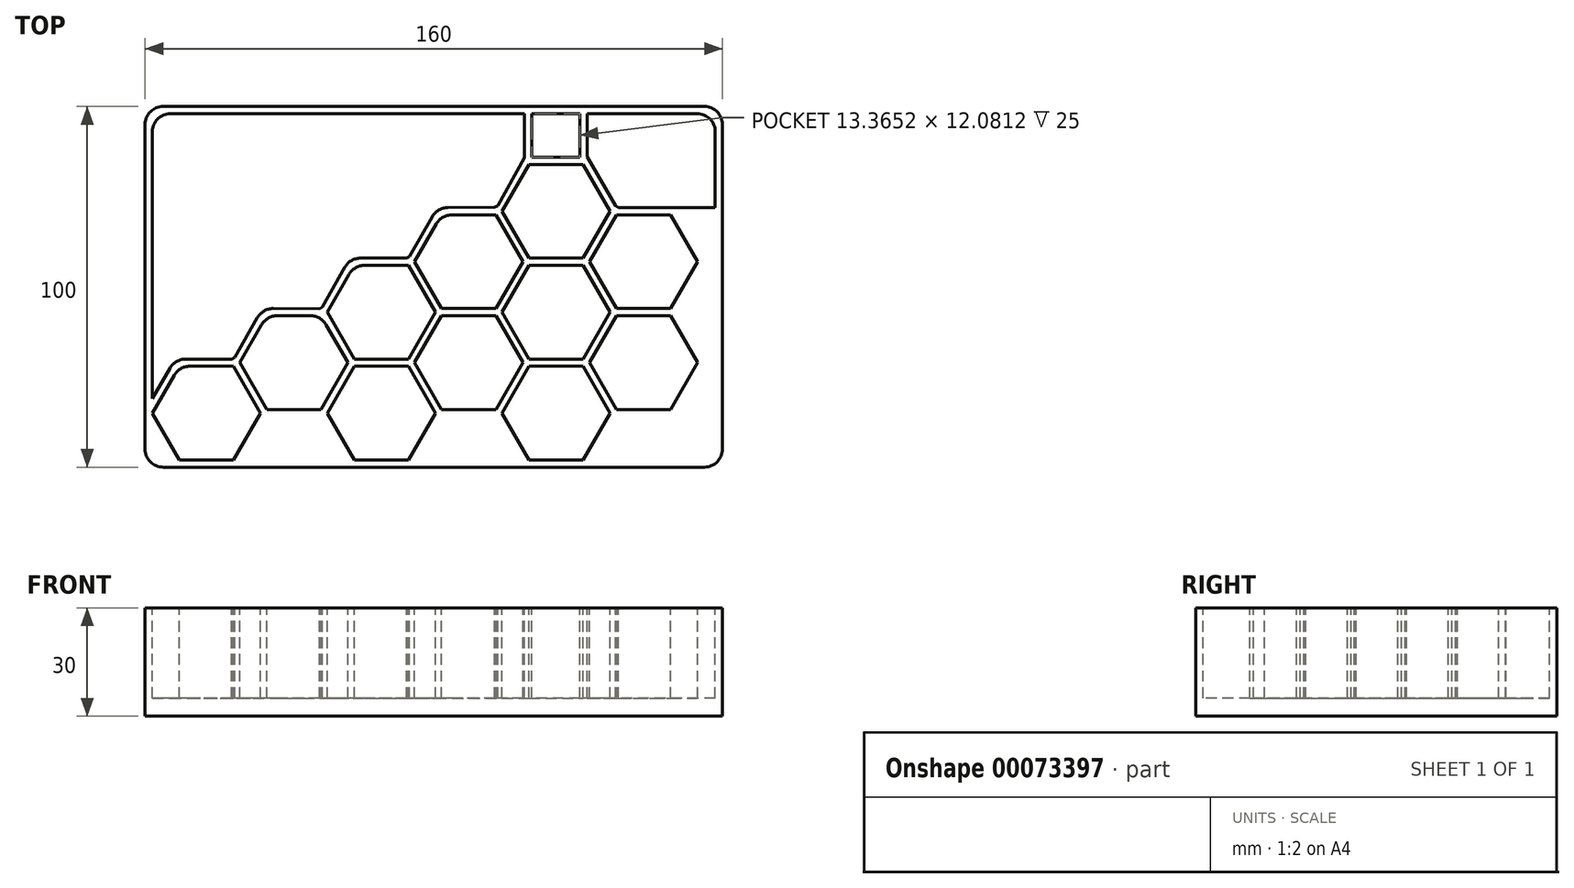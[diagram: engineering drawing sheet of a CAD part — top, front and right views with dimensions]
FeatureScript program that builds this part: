
annotation { "Feature Type Name" : "Feature", "Feature Type Description" : "" }
export const myFeature = defineFeature(function(context is Context, id is Id, definition is map)
    precondition{}
    {
        {
            var Q0;
            Q0=qCreatedBy(makeId("Top.planeOp"),FACE);
            var sketch = newSketch(context, id + "F0", { "sketchPlane" : qUnion([Q0])});
            skLineSegment(sketch, "E0.rect.bottom", {"start": v(80, 50) * mm, "end": v(-80, 50) * mm});
            skLineSegment(sketch, "E0.rect.top", {"start": v(80, -50) * mm, "end": v(-80, -50) * mm});
            skLineSegment(sketch, "E0.rect.left", {"start": v(80, 50) * mm, "end": v(80, -50) * mm});
            skLineSegment(sketch, "E0.rect.right", {"start": v(-80, 50) * mm, "end": v(-80, -50) * mm});
            skPoint(sketch, "E0.rect.middle", {"position": v(0, 0) * mm});
            skSolve(sketch);
        }
        {
            var Q0;
            Q0=makeQuery(id+"F0.imprint","IMPRINT",FACE,{"disambiguationData":[TD([[makeQuery(id+"F0.imprint","IMPRINT",EDGE,{"derivedFrom":sQuery(id+"F0.wireOp",EDGE,"E0.rect.bottom")}),1.0]])]});
            extrude(context, id + "F1", {"entities" : qUnion([Q0]), "depth" : 30 * mm});
        }
        {
            var Q0;
            Q0=makeQuery(id+"F1.opExtrude","CAP_FACE",FACE,{"disambiguationData":[OSD([sQuery(id+"F0.wireOp",EDGE,"E0.rect.bottom"),sQuery(id+"F0.wireOp",EDGE,"E0.rect.top"),sQuery(id+"F0.wireOp",EDGE,"E0.rect.left"),sQuery(id+"F0.wireOp",EDGE,"E0.rect.right")])],"isStart":false});
            var sketch = newSketch(context, id + "F2", { "sketchPlane" : qUnion([Q0])});
            skCircle(sketch, "E1.cCircle", {"center": v(-63, -35) * mm, "radius": 13 * mm, "construction": true});
            skLineSegment(sketch, "E1.0", {"start": v(-55.5, -48) * mm, "end": v(-70.5, -48) * mm});
            skLineSegment(sketch, "E1.1", {"start": v(-70.5, -48) * mm, "end": v(-78, -35) * mm});
            skLineSegment(sketch, "E1.2", {"start": v(-78, -35) * mm, "end": v(-70.5, -22.02) * mm});
            skLineSegment(sketch, "E1.3", {"start": v(-70.5, -22.02) * mm, "end": v(-55.5, -22.02) * mm});
            skLineSegment(sketch, "E1.4", {"start": v(-55.5, -22.02) * mm, "end": v(-48, -35) * mm});
            skLineSegment(sketch, "E1.5", {"start": v(-48, -35) * mm, "end": v(-55.5, -48) * mm});
            skPoint(sketch, "E1.0.midPoint", {"position": v(-63, -48) * mm});
            skLineSegment(sketch, "E2.0.1.0", {"start": v(-46.27, -8.03) * mm, "end": v(-31.27, -8.03) * mm});
            skLineSegment(sketch, "E2.0.1.1", {"start": v(-31.27, -8.03) * mm, "end": v(-23.77, -21.02) * mm});
            skLineSegment(sketch, "E2.0.1.2", {"start": v(-23.77, -21.02) * mm, "end": v(-31.27, -34) * mm});
            skLineSegment(sketch, "E2.0.1.3", {"start": v(-31.27, -34) * mm, "end": v(-46.27, -34) * mm});
            skLineSegment(sketch, "E2.0.1.4", {"start": v(-46.27, -34) * mm, "end": v(-53.77, -21.02) * mm});
            skLineSegment(sketch, "E2.0.1.5", {"start": v(-53.77, -21.02) * mm, "end": v(-46.27, -8.03) * mm});
            skLineSegment(sketch, "E2.0.2.0", {"start": v(-22.04, 5.96) * mm, "end": v(-7.04, 5.96) * mm});
            skLineSegment(sketch, "E2.0.2.1", {"start": v(-7.04, 5.96) * mm, "end": v(0.46, -7.03) * mm});
            skLineSegment(sketch, "E2.0.2.2", {"start": v(0.46, -7.03) * mm, "end": v(-7.04, -20.02) * mm});
            skLineSegment(sketch, "E2.0.2.3", {"start": v(-7.04, -20.02) * mm, "end": v(-22.04, -20.02) * mm});
            skLineSegment(sketch, "E2.0.2.4", {"start": v(-22.04, -20.02) * mm, "end": v(-29.54, -7.03) * mm});
            skLineSegment(sketch, "E2.0.2.5", {"start": v(-29.54, -7.03) * mm, "end": v(-22.04, 5.96) * mm});
            skLineSegment(sketch, "E2.0.3.0", {"start": v(2.2, 19.95) * mm, "end": v(17.2, 19.95) * mm});
            skLineSegment(sketch, "E2.0.3.1", {"start": v(17.2, 19.95) * mm, "end": v(24.7, 6.96) * mm});
            skLineSegment(sketch, "E2.0.3.2", {"start": v(24.7, 6.96) * mm, "end": v(17.2, -6.03) * mm});
            skLineSegment(sketch, "E2.0.3.3", {"start": v(17.2, -6.03) * mm, "end": v(2.2, -6.03) * mm});
            skLineSegment(sketch, "E2.0.3.4", {"start": v(2.2, -6.03) * mm, "end": v(-5.3, 6.96) * mm});
            skLineSegment(sketch, "E2.0.3.5", {"start": v(-5.3, 6.96) * mm, "end": v(2.2, 19.95) * mm});
            skLineSegment(sketch, "E2.0.4.0", {"start": v(26.43, 33.94) * mm, "end": v(41.43, 33.94) * mm});
            skLineSegment(sketch, "E2.0.4.1", {"start": v(41.43, 33.94) * mm, "end": v(48.93, 20.95) * mm});
            skLineSegment(sketch, "E2.0.4.2", {"start": v(48.93, 20.95) * mm, "end": v(41.43, 7.96) * mm});
            skLineSegment(sketch, "E2.0.4.3", {"start": v(41.43, 7.96) * mm, "end": v(26.43, 7.96) * mm});
            skLineSegment(sketch, "E2.0.4.4", {"start": v(26.43, 7.96) * mm, "end": v(18.93, 20.95) * mm});
            skLineSegment(sketch, "E2.0.4.5", {"start": v(18.93, 20.95) * mm, "end": v(26.43, 33.94) * mm});
            skLineSegment(sketch, "E2.1.0.0", {"start": v(-22.04, -22.02) * mm, "end": v(-7.04, -22.02) * mm});
            skLineSegment(sketch, "E2.1.0.1", {"start": v(-7.04, -22.02) * mm, "end": v(0.46, -35) * mm});
            skLineSegment(sketch, "E2.1.0.2", {"start": v(0.46, -35) * mm, "end": v(-7.04, -48) * mm});
            skLineSegment(sketch, "E2.1.0.3", {"start": v(-7.04, -48) * mm, "end": v(-22.04, -48) * mm});
            skLineSegment(sketch, "E2.1.0.4", {"start": v(-22.04, -48) * mm, "end": v(-29.54, -35) * mm});
            skLineSegment(sketch, "E2.1.0.5", {"start": v(-29.54, -35) * mm, "end": v(-22.04, -22.02) * mm});
            skLineSegment(sketch, "E2.1.1.0", {"start": v(2.2, -8.03) * mm, "end": v(17.2, -8.03) * mm});
            skLineSegment(sketch, "E2.1.1.1", {"start": v(17.2, -8.03) * mm, "end": v(24.7, -21.02) * mm});
            skLineSegment(sketch, "E2.1.1.2", {"start": v(24.7, -21.02) * mm, "end": v(17.2, -34) * mm});
            skLineSegment(sketch, "E2.1.1.3", {"start": v(17.2, -34) * mm, "end": v(2.2, -34) * mm});
            skLineSegment(sketch, "E2.1.1.4", {"start": v(2.2, -34) * mm, "end": v(-5.3, -21.02) * mm});
            skLineSegment(sketch, "E2.1.1.5", {"start": v(-5.3, -21.02) * mm, "end": v(2.2, -8.03) * mm});
            skLineSegment(sketch, "E2.1.2.0", {"start": v(26.43, 5.96) * mm, "end": v(41.43, 5.96) * mm});
            skLineSegment(sketch, "E2.1.2.1", {"start": v(41.43, 5.96) * mm, "end": v(48.93, -7.03) * mm});
            skLineSegment(sketch, "E2.1.2.2", {"start": v(48.93, -7.03) * mm, "end": v(41.43, -20.02) * mm});
            skLineSegment(sketch, "E2.1.2.3", {"start": v(41.43, -20.02) * mm, "end": v(26.43, -20.02) * mm});
            skLineSegment(sketch, "E2.1.2.4", {"start": v(26.43, -20.02) * mm, "end": v(18.93, -7.03) * mm});
            skLineSegment(sketch, "E2.1.2.5", {"start": v(18.93, -7.03) * mm, "end": v(26.43, 5.96) * mm});
            skLineSegment(sketch, "E2.1.3.0", {"start": v(50.66, 19.95) * mm, "end": v(65.66, 19.95) * mm});
            skLineSegment(sketch, "E2.1.3.1", {"start": v(65.66, 19.95) * mm, "end": v(73.16, 6.96) * mm});
            skLineSegment(sketch, "E2.1.3.2", {"start": v(73.16, 6.96) * mm, "end": v(65.66, -6.03) * mm});
            skLineSegment(sketch, "E2.1.3.3", {"start": v(65.66, -6.03) * mm, "end": v(50.66, -6.03) * mm});
            skLineSegment(sketch, "E2.1.3.4", {"start": v(50.66, -6.03) * mm, "end": v(43.16, 6.96) * mm});
            skLineSegment(sketch, "E2.1.3.5", {"start": v(43.16, 6.96) * mm, "end": v(50.66, 19.95) * mm});
            skLineSegment(sketch, "E2.2.0.0", {"start": v(26.43, -22.02) * mm, "end": v(41.43, -22.02) * mm});
            skLineSegment(sketch, "E2.2.0.1", {"start": v(41.43, -22.02) * mm, "end": v(48.93, -35) * mm});
            skLineSegment(sketch, "E2.2.0.2", {"start": v(48.93, -35) * mm, "end": v(41.43, -48) * mm});
            skLineSegment(sketch, "E2.2.0.3", {"start": v(41.43, -48) * mm, "end": v(26.43, -48) * mm});
            skLineSegment(sketch, "E2.2.0.4", {"start": v(26.43, -48) * mm, "end": v(18.93, -35) * mm});
            skLineSegment(sketch, "E2.2.0.5", {"start": v(18.93, -35) * mm, "end": v(26.43, -22.02) * mm});
            skLineSegment(sketch, "E2.2.1.0", {"start": v(50.66, -8.03) * mm, "end": v(65.66, -8.03) * mm});
            skLineSegment(sketch, "E2.2.1.1", {"start": v(65.66, -8.03) * mm, "end": v(73.16, -21.02) * mm});
            skLineSegment(sketch, "E2.2.1.2", {"start": v(73.16, -21.02) * mm, "end": v(65.66, -34) * mm});
            skLineSegment(sketch, "E2.2.1.3", {"start": v(65.66, -34) * mm, "end": v(50.66, -34) * mm});
            skLineSegment(sketch, "E2.2.1.4", {"start": v(50.66, -34) * mm, "end": v(43.16, -21.02) * mm});
            skLineSegment(sketch, "E2.2.1.5", {"start": v(43.16, -21.02) * mm, "end": v(50.66, -8.03) * mm});
            skLineSegment(sketch, "E2.direction1", {"start": v(-70.5, -22.02) * mm, "end": v(-22.04, -22.02) * mm, "construction": true});
            skLineSegment(sketch, "E2.direction2", {"start": v(-70.5, -22.02) * mm, "end": v(-46.27, -8.03) * mm, "construction": true});
            skSolve(sketch);
        }
        {
            var Q0;
            Q0 = qSketchRegion(id + "F2", true);
            extrude(context, id + "F3", {"entities" : qUnion([Q0]), "operationType" : NewBodyOperationType.REMOVE, "oppositeDirection" : true, "depth" : 25 * mm});
        }
        {
            var Q0;
            Q0=makeQuery(id+"F1.opExtrude","CAP_FACE",FACE,{"disambiguationData":[OSD([sQuery(id+"F0.wireOp",EDGE,"E0.rect.bottom"),sQuery(id+"F0.wireOp",EDGE,"E0.rect.top"),sQuery(id+"F0.wireOp",EDGE,"E0.rect.left"),sQuery(id+"F0.wireOp",EDGE,"E0.rect.right")])],"isStart":false});
            var sketch = newSketch(context, id + "F4", { "sketchPlane" : qUnion([Q0])});
            skLineSegment(sketch, "E3", {"start": v(-70.5, -22.02) * mm, "end": v(-55.5, -22.02) * mm, "construction": true});
            skLineSegment(sketch, "E4", {"start": v(-55.5, -22.02) * mm, "end": v(-53.69, -21.07) * mm, "construction": true});
            skLineSegment(sketch, "E5", {"start": v(-53.69, -21.07) * mm, "end": v(-46.27, -8.03) * mm, "construction": true});
            skLineSegment(sketch, "E6", {"start": v(-46.27, -8.03) * mm, "end": v(-31.08, -8.11) * mm, "construction": true});
            skLineSegment(sketch, "E7", {"start": v(-31.08, -8.11) * mm, "end": v(-29.4, -7) * mm, "construction": true});
            skLineSegment(sketch, "E8", {"start": v(-29.4, -7) * mm, "end": v(-22.04, 5.96) * mm, "construction": true});
            skLineSegment(sketch, "E9", {"start": v(-22.04, 5.96) * mm, "end": v(-7.04, 5.96) * mm, "construction": true});
            skLineSegment(sketch, "E10", {"start": v(-7.04, 5.96) * mm, "end": v(-5.3, 6.96) * mm, "construction": true});
            skLineSegment(sketch, "E11", {"start": v(-5.3, 6.96) * mm, "end": v(2.2, 19.95) * mm, "construction": true});
            skLineSegment(sketch, "E12", {"start": v(2.2, 19.95) * mm, "end": v(17.29, 20.1) * mm, "construction": true});
            skLineSegment(sketch, "E13", {"start": v(17.29, 20.1) * mm, "end": v(19.15, 20.84) * mm, "construction": true});
            skLineSegment(sketch, "E14", {"start": v(19.15, 20.84) * mm, "end": v(26.43, 33.94) * mm, "construction": true});
            skLineSegment(sketch, "E15", {"start": v(26.43, 33.94) * mm, "end": v(41.43, 33.94) * mm, "construction": true});
            skLineSegment(sketch, "E16", {"start": v(41.43, 33.94) * mm, "end": v(48.93, 20.95) * mm, "construction": true});
            skLineSegment(sketch, "E17", {"start": v(48.93, 20.95) * mm, "end": v(50.66, 19.95) * mm, "construction": true});
            skLineSegment(sketch, "E18", {"start": v(50.66, 19.95) * mm, "end": v(80, 19.95) * mm, "construction": true});
            skLineSegment(sketch, "E19", {"start": v(80, 19.95) * mm, "end": v(80, 50) * mm, "construction": true});
            skLineSegment(sketch, "E20", {"start": v(80, 50) * mm, "end": v(-80, 50) * mm, "construction": true});
            skLineSegment(sketch, "E21", {"start": v(-80, 50) * mm, "end": v(-80, -34.9) * mm, "construction": true});
            skLineSegment(sketch, "E22", {"start": v(-80, -34.9) * mm, "end": v(-78, -35) * mm, "construction": true});
            skLineSegment(sketch, "E23", {"start": v(-78, -35) * mm, "end": v(-70.5, -22.02) * mm, "construction": true});
            skLineSegment(sketch, "E24.0", {"start": v(78, 21.95) * mm, "end": v(78, 48) * mm});
            skLineSegment(sketch, "E24.1", {"start": v(51.2, 21.95) * mm, "end": v(78, 21.95) * mm});
            skLineSegment(sketch, "E24.2", {"start": v(50.4, 22.42) * mm, "end": v(51.2, 21.95) * mm});
            skLineSegment(sketch, "E24.3", {"start": v(42.55, 36) * mm, "end": v(50.4, 22.42) * mm});
            skLineSegment(sketch, "E24.5", {"start": v(78, 48) * mm, "end": v(42.55, 48) * mm});
            skLineSegment(sketch, "E24.6", {"start": v(17.74, 22.43) * mm, "end": v(25.18, 35.82) * mm});
            skLineSegment(sketch, "E24.7", {"start": v(16.9, 22.1) * mm, "end": v(17.74, 22.43) * mm});
            skLineSegment(sketch, "E24.8", {"start": v(1.04, 21.94) * mm, "end": v(16.9, 22.1) * mm});
            skLineSegment(sketch, "E24.9", {"start": v(-6.77, 8.43) * mm, "end": v(1.04, 21.94) * mm});
            skLineSegment(sketch, "E24.10", {"start": v(-55.99, -20.02) * mm, "end": v(-55.13, -19.57) * mm});
            skLineSegment(sketch, "E24.11", {"start": v(-71.65, -20.02) * mm, "end": v(-55.99, -20.02) * mm});
            skLineSegment(sketch, "E24.12", {"start": v(-78, -31) * mm, "end": v(-71.65, -20.02) * mm});
            skLineSegment(sketch, "E24.13", {"start": v(-78, 48) * mm, "end": v(-78, -31) * mm});
            skLineSegment(sketch, "E24.14", {"start": v(-55.13, -19.57) * mm, "end": v(-47.43, -6.02) * mm});
            skLineSegment(sketch, "E24.15", {"start": v(-47.43, -6.02) * mm, "end": v(-31.68, -6.1) * mm});
            skLineSegment(sketch, "E24.16", {"start": v(-31.68, -6.1) * mm, "end": v(-30.91, -5.6) * mm});
            skLineSegment(sketch, "E24.17", {"start": v(-30.91, -5.6) * mm, "end": v(-23.2, 7.96) * mm});
            skLineSegment(sketch, "E24.18", {"start": v(-23.2, 7.96) * mm, "end": v(-7.57, 7.96) * mm});
            skLineSegment(sketch, "E24.19", {"start": v(-7.57, 7.96) * mm, "end": v(-6.77, 8.43) * mm});
            skLineSegment(sketch, "E25", {"start": v(25.18, 35.82) * mm, "end": v(25.18, 48) * mm});
            skLineSegment(sketch, "E26", {"start": v(42.55, 36) * mm, "end": v(42.55, 48) * mm});
            skLineSegment(sketch, "E27.trimOffspring", {"start": v(25.18, 48) * mm, "end": v(-78, 48) * mm});
            skLineSegment(sketch, "E28.bottom", {"start": v(27.18, 48.02) * mm, "end": v(40.55, 48.02) * mm});
            skLineSegment(sketch, "E28.top", {"start": v(27.18, 35.94) * mm, "end": v(40.55, 35.94) * mm});
            skLineSegment(sketch, "E28.left", {"start": v(27.18, 48.02) * mm, "end": v(27.18, 35.94) * mm});
            skLineSegment(sketch, "E28.right", {"start": v(40.55, 48.02) * mm, "end": v(40.55, 35.94) * mm});
            skLineSegment(sketch, "E29", {"start": v(33.93, 35.94) * mm, "end": v(33.93, 33.94) * mm});
            skPoint(sketch, "E29.startSnap0", {"position": v(33.93, 33.94) * mm});
            skSolve(sketch);
        }
        {
            var Q0;
            Q0 = qSketchRegion(id + "F4", true);
            var Q1;
            Q1=makeQuery(id+"F3.boolean.opBoolean","COPY",FACE,{"derivedFrom":makeQuery(id+"F3.opExtrude","CAP_FACE",FACE,{"disambiguationData":[OSD([sQuery(id+"F2.wireOp",EDGE,"E2.0.2.0"),sQuery(id+"F2.wireOp",EDGE,"E2.0.2.1"),sQuery(id+"F2.wireOp",EDGE,"E2.0.2.2"),sQuery(id+"F2.wireOp",EDGE,"E2.0.2.3"),sQuery(id+"F2.wireOp",EDGE,"E2.0.2.4"),sQuery(id+"F2.wireOp",EDGE,"E2.0.2.5")])],"isStart":false})});
            extrude(context, id + "F5", {"entities" : qUnion([Q0]), "operationType" : NewBodyOperationType.REMOVE, "endBound" : BoundingType.UP_TO_SURFACE, "oppositeDirection" : true, "endBoundEntityFace" : qUnion([Q1]), "depth" : 25 * mm});
        }
        {
            var Q0;
            Q0=makeQuery(id+"F3.boolean.opBoolean","COPY",EDGE,{"derivedFrom":makeQuery(id+"F3.opExtrude","SWEPT_EDGE",EDGE,{"disambiguationData":[OSD([sQuery(id+"F2.wireOp",EDGE,"E2.0.1.0"),sQuery(id+"F2.wireOp",EDGE,"E2.0.1.5")])]})});
            var Q1;
            Q1=makeQuery(id+"F3.boolean.opBoolean","COPY",EDGE,{"derivedFrom":makeQuery(id+"F3.opExtrude","SWEPT_EDGE",EDGE,{"disambiguationData":[OSD([sQuery(id+"F2.wireOp",EDGE,"E2.0.1.0"),sQuery(id+"F2.wireOp",EDGE,"E2.0.1.1")])]})});
            fillet(context, id + "F6", {"entities" : qUnion([Q0, Q1]), "radius" : 5 * mm, "tangentPropagation" : true, "allowEdgeOverflow" : false});
        }
        {
            var Q0;
            Q0=makeQuery(id+"F1.opExtrude","SWEPT_EDGE",EDGE,{"disambiguationData":[OSD([sQuery(id+"F0.wireOp",EDGE,"E0.rect.top"),sQuery(id+"F0.wireOp",EDGE,"E0.rect.right")])]});
            var Q1;
            Q1=makeQuery(id+"F1.opExtrude","SWEPT_EDGE",EDGE,{"disambiguationData":[OSD([sQuery(id+"F0.wireOp",EDGE,"E0.rect.top"),sQuery(id+"F0.wireOp",EDGE,"E0.rect.left")])]});
            var Q2;
            Q2=makeQuery(id+"F1.opExtrude","SWEPT_EDGE",EDGE,{"disambiguationData":[OSD([sQuery(id+"F0.wireOp",EDGE,"E0.rect.bottom"),sQuery(id+"F0.wireOp",EDGE,"E0.rect.left")])]});
            var Q3;
            Q3=makeQuery(id+"F1.opExtrude","SWEPT_EDGE",EDGE,{"disambiguationData":[OSD([sQuery(id+"F0.wireOp",EDGE,"E0.rect.bottom"),sQuery(id+"F0.wireOp",EDGE,"E0.rect.right")])]});
            var Q4;
            Q4=makeQuery(id+"F5.boolean.opBoolean","COPY",EDGE,{"derivedFrom":makeQuery(id+"F5.opExtrude","SWEPT_EDGE",EDGE,{"disambiguationData":[OSD([sQuery(id+"F4.wireOp",EDGE,"E24.13"),sQuery(id+"F4.wireOp",EDGE,"E27.trimOffspring")])]})});
            var Q5;
            Q5=makeQuery(id+"F5.boolean.opBoolean","COPY",EDGE,{"derivedFrom":makeQuery(id+"F5.opExtrude","SWEPT_EDGE",EDGE,{"disambiguationData":[OSD([sQuery(id+"F4.wireOp",EDGE,"E24.0"),sQuery(id+"F4.wireOp",EDGE,"E24.5")])]})});
            fillet(context, id + "F7", {"entities" : qUnion([Q0, Q1, Q2, Q3, Q4, Q5]), "radius" : 5 * mm, "tangentPropagation" : true, "allowEdgeOverflow" : false});
        }
        {
            var Q0;
            Q0=makeQuery(id+"F5.boolean.opBoolean","COPY",EDGE,{"derivedFrom":makeQuery(id+"F5.opExtrude","SWEPT_EDGE",EDGE,{"disambiguationData":[OSD([sQuery(id+"F4.wireOp",EDGE,"E24.17"),sQuery(id+"F4.wireOp",EDGE,"E24.18")])]})});
            var Q1;
            Q1=makeQuery(id+"F5.boolean.opBoolean","COPY",EDGE,{"derivedFrom":makeQuery(id+"F5.opExtrude","SWEPT_EDGE",EDGE,{"disambiguationData":[OSD([sQuery(id+"F4.wireOp",EDGE,"E24.8"),sQuery(id+"F4.wireOp",EDGE,"E24.9")])]})});
            var Q2;
            Q2=makeQuery(id+"F5.boolean.opBoolean","COPY",EDGE,{"derivedFrom":makeQuery(id+"F5.opExtrude","SWEPT_EDGE",EDGE,{"disambiguationData":[OSD([sQuery(id+"F4.wireOp",EDGE,"E24.14"),sQuery(id+"F4.wireOp",EDGE,"E24.15")])]})});
            var Q3;
            Q3=makeQuery(id+"F5.boolean.opBoolean","COPY",EDGE,{"derivedFrom":makeQuery(id+"F5.opExtrude","SWEPT_EDGE",EDGE,{"disambiguationData":[OSD([sQuery(id+"F4.wireOp",EDGE,"E24.11"),sQuery(id+"F4.wireOp",EDGE,"E24.12")])]})});
            var Q4;
            Q4=makeQuery(id+"F3.boolean.opBoolean","COPY",EDGE,{"derivedFrom":makeQuery(id+"F3.opExtrude","SWEPT_EDGE",EDGE,{"disambiguationData":[OSD([sQuery(id+"F2.wireOp",EDGE,"E1.2"),sQuery(id+"F2.wireOp",EDGE,"E1.3")])]})});
            var Q5;
            Q5=makeQuery(id+"F3.boolean.opBoolean","COPY",EDGE,{"derivedFrom":makeQuery(id+"F3.opExtrude","SWEPT_EDGE",EDGE,{"disambiguationData":[OSD([sQuery(id+"F2.wireOp",EDGE,"E2.0.2.0"),sQuery(id+"F2.wireOp",EDGE,"E2.0.2.5")])]})});
            var Q6;
            Q6=makeQuery(id+"F3.boolean.opBoolean","COPY",EDGE,{"derivedFrom":makeQuery(id+"F3.opExtrude","SWEPT_EDGE",EDGE,{"disambiguationData":[OSD([sQuery(id+"F2.wireOp",EDGE,"E2.0.3.0"),sQuery(id+"F2.wireOp",EDGE,"E2.0.3.5")])]})});
            fillet(context, id + "F8", {"entities" : qUnion([Q0, Q1, Q2, Q3, Q4, Q5, Q6]), "radius" : 5 * mm, "tangentPropagation" : true, "allowEdgeOverflow" : false});
        }
    });
